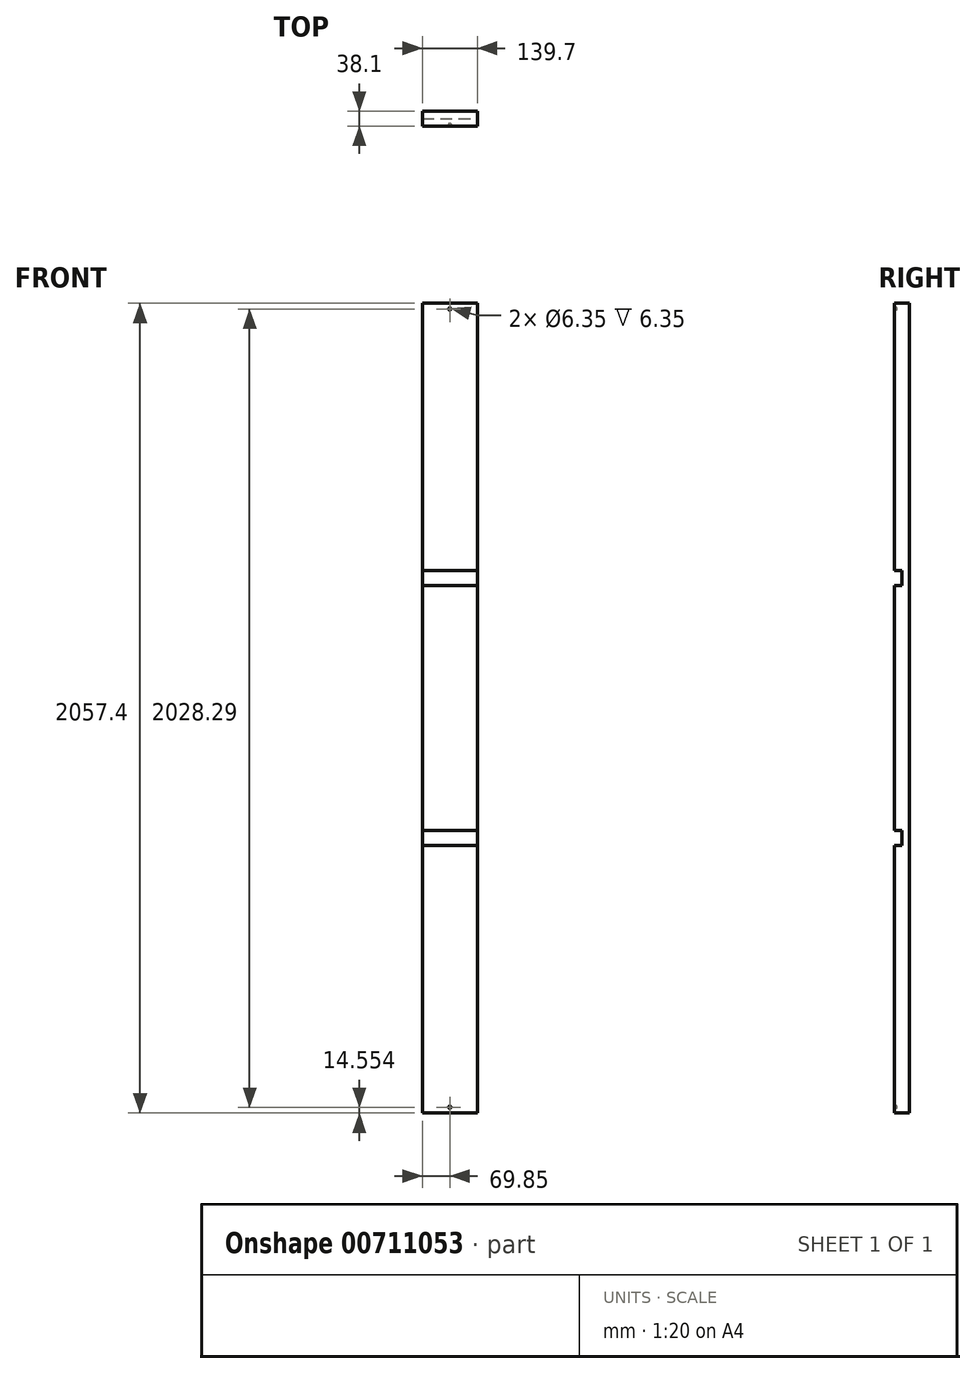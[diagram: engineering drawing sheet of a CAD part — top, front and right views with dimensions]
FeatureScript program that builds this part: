
annotation { "Feature Type Name" : "Feature", "Feature Type Description" : "" }
export const myFeature = defineFeature(function(context is Context, id is Id, definition is map)
    precondition{}
    {
        {
            var Q0;
            Q0=qCreatedBy(makeId("Top.planeOp"),FACE);
            var sketch = newSketch(context, id + "F0", { "sketchPlane" : qUnion([Q0])});
            skLineSegment(sketch, "E0.bottom", {"start": v(69.85, 19.05) * mm, "end": v(-69.85, 19.05) * mm});
            skLineSegment(sketch, "E0.top", {"start": v(69.85, -19.05) * mm, "end": v(-69.85, -19.05) * mm});
            skLineSegment(sketch, "E0.left", {"start": v(69.85, 19.05) * mm, "end": v(69.85, -19.05) * mm});
            skLineSegment(sketch, "E0.right", {"start": v(-69.85, 19.05) * mm, "end": v(-69.85, -19.05) * mm});
            skPoint(sketch, "E0.middle", {"position": v(0, 0) * mm});
            skSolve(sketch);
        }
        {
            var Q0;
            Q0=makeQuery(id+"F0.imprint","IMPRINT",FACE,{"disambiguationData":[TD([[makeQuery(id+"F0.imprint","IMPRINT",EDGE,{"derivedFrom":sQuery(id+"F0.wireOp",EDGE,"E0.bottom")}),1.0]])]});
            extrude(context, id + "F1", {"entities" : qUnion([Q0]), "depth" : 2057.4 * mm, "offsetDistance" : 25.4 * mm});
        }
        {
            var Q0;
            Q0=makeQuery(id+"F1.opExtrude","SWEPT_FACE",FACE,{"disambiguationData":[OSD([sQuery(id+"F0.wireOp",EDGE,"E0.left")])]});
            var sketch = newSketch(context, id + "F2", { "sketchPlane" : qUnion([Q0])});
            skLineSegment(sketch, "E1.0", {"start": v(-19.05, 717.55) * mm, "end": v(0, 717.55) * mm});
            skLineSegment(sketch, "E2.0", {"start": v(-19.05, 1339.85) * mm, "end": v(0, 1339.85) * mm});
            skLineSegment(sketch, "E3.0", {"start": v(-19.05, 1377.95) * mm, "end": v(0, 1377.95) * mm});
            skLineSegment(sketch, "E4.0", {"start": v(-19.05, 679.45) * mm, "end": v(0, 679.45) * mm});
            skLineSegment(sketch, "E5.0", {"start": v(0, 1377.95) * mm, "end": v(0, 1339.85) * mm});
            skLineSegment(sketch, "E6.trimOffspring", {"start": v(0, 717.55) * mm, "end": v(0, 679.45) * mm});
            skPoint(sketch, "E7.end.orphan", {"position": v(19.05, 1028.7) * mm});
            skPoint(sketch, "E7.start.orphan", {"position": v(-19.05, 1028.7) * mm});
            skSolve(sketch);
        }
        {
            var Q0;
            Q0 = qSketchRegion(id + "F2", true);
            var Q1;
            {var subQ0=sQuery(id+"F2.wireOp",EDGE,"E1.0");Q1=makeQuery(id+"F2.imprint","IMPRINT",FACE,{"disambiguationData":[TD([[makeQuery(id+"F2.imprint","IMPRINT",EDGE,{"derivedFrom":subQ0}),-1.0]])]});}
            var Q2;
            {var subQ0=sQuery(id+"F2.wireOp",EDGE,"E2.0");Q2=makeQuery(id+"F2.imprint","IMPRINT",FACE,{"disambiguationData":[TD([[makeQuery(id+"F2.imprint","IMPRINT",EDGE,{"derivedFrom":subQ0}),1.0]])]});}
            extrude(context, id + "F3", {"entities" : qUnion([Q0, Q1, Q2]), "operationType" : NewBodyOperationType.REMOVE, "oppositeDirection" : true, "depth" : 139.7 * mm, "offsetDistance" : 25.4 * mm});
        }
        {
            var Q0;
            {var subQ2=sQuery(id+"F0.wireOp",EDGE,"E0.top");Q0=makeQuery(id+"F3.boolean.opBoolean","SPLIT",FACE,{"disambiguationData":[TD([makeQuery(id+"F3.opExtrude","SWEPT_FACE",FACE,{"disambiguationData":[OSD([sQuery(id+"F2.wireOp",EDGE,"E3.0")])]})])],"derivedFrom":makeQuery(id+"F1.opExtrude","SWEPT_FACE",FACE,{"disambiguationData":[OSD([subQ2])]})});}
            var sketch = newSketch(context, id + "F4", { "sketchPlane" : qUnion([Q0])});
            skLineSegment(sketch, "E8.0", {"start": v(69.85, 2042.85) * mm, "end": v(-69.85, 2042.85) * mm});
            skCircle(sketch, "E9", {"center": v(0, 2042.85) * mm, "radius": 3.18 * mm});
            skSolve(sketch);
        }
        {
            var Q0;
            Q0 = qSketchRegion(id + "F4", true);
            extrude(context, id + "F5", {"entities" : qUnion([Q0]), "operationType" : NewBodyOperationType.REMOVE, "oppositeDirection" : true, "depth" : 6.35 * mm, "offsetDistance" : 25.4 * mm});
        }
        {
            var Q0;
            {var subQ2=sQuery(id+"F0.wireOp",EDGE,"E0.top");Q0=makeQuery(id+"F3.boolean.opBoolean","SPLIT",FACE,{"disambiguationData":[TD([makeQuery(id+"F3.opExtrude","SWEPT_FACE",FACE,{"disambiguationData":[OSD([sQuery(id+"F2.wireOp",EDGE,"E4.0")])]})])],"derivedFrom":makeQuery(id+"F1.opExtrude","SWEPT_FACE",FACE,{"disambiguationData":[OSD([subQ2])]})});}
            var sketch = newSketch(context, id + "F6", { "sketchPlane" : qUnion([Q0])});
            skLineSegment(sketch, "E10.0", {"start": v(69.85, 14.55) * mm, "end": v(-69.85, 14.55) * mm});
            skCircle(sketch, "E11", {"center": v(0, 14.55) * mm, "radius": 3.18 * mm});
            skSolve(sketch);
        }
        {
            var Q0;
            Q0 = qSketchRegion(id + "F6", true);
            extrude(context, id + "F7", {"entities" : qUnion([Q0]), "operationType" : NewBodyOperationType.REMOVE, "oppositeDirection" : true, "depth" : 6.35 * mm, "offsetDistance" : 25.4 * mm});
        }
    });
